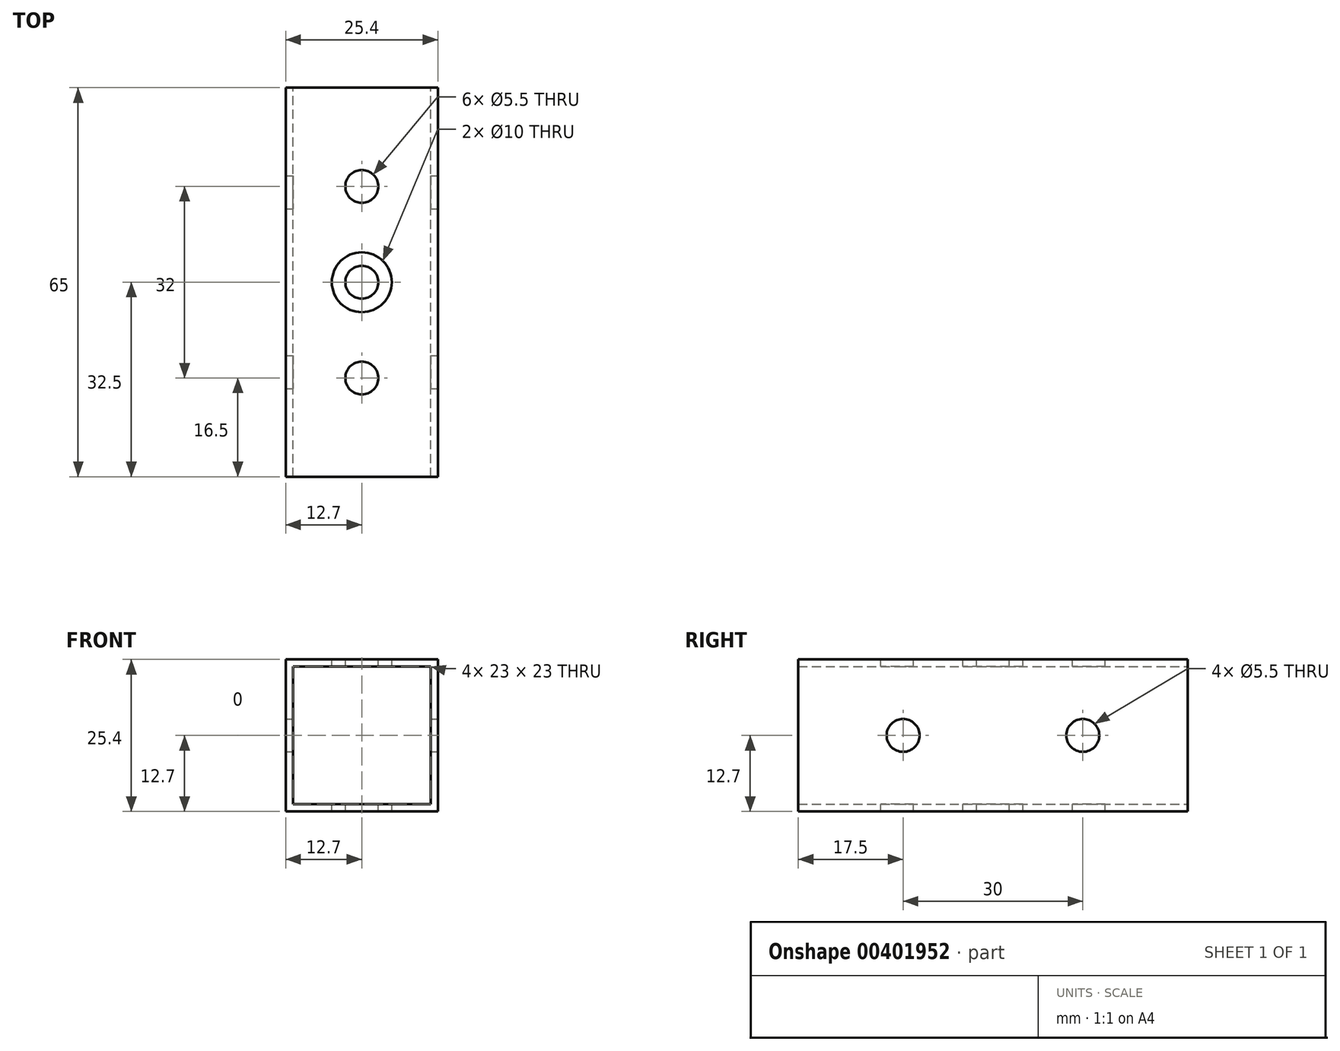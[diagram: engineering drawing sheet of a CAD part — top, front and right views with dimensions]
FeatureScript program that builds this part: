
annotation { "Feature Type Name" : "Feature", "Feature Type Description" : "" }
export const myFeature = defineFeature(function(context is Context, id is Id, definition is map)
    precondition{}
    {
        {
            var Q0;
            Q0=qCreatedBy(makeId("Front.planeOp"),FACE);
            var sketch = newSketch(context, id + "F0", { "sketchPlane" : qUnion([Q0])});
            skLineSegment(sketch, "E0.bottom", {"start": v(-12.7, 12.7) * mm, "end": v(12.7, 12.7) * mm});
            skLineSegment(sketch, "E0.top", {"start": v(-12.7, -12.7) * mm, "end": v(12.7, -12.7) * mm});
            skLineSegment(sketch, "E0.left", {"start": v(-12.7, 12.7) * mm, "end": v(-12.7, -12.7) * mm});
            skLineSegment(sketch, "E0.right", {"start": v(12.7, 12.7) * mm, "end": v(12.7, -12.7) * mm});
            skLineSegment(sketch, "E1", {"start": v(0, 0) * mm, "end": v(0, 12.7) * mm, "construction": true});
            skLineSegment(sketch, "E2", {"start": v(0, 0) * mm, "end": v(-12.7, 0) * mm, "construction": true});
            skLineSegment(sketch, "E3.0", {"start": v(-11.5, -11.5) * mm, "end": v(11.5, -11.5) * mm});
            skLineSegment(sketch, "E3.1", {"start": v(-11.5, 11.5) * mm, "end": v(-11.5, -11.5) * mm});
            skLineSegment(sketch, "E3.2", {"start": v(-11.5, 11.5) * mm, "end": v(11.5, 11.5) * mm});
            skLineSegment(sketch, "E3.3", {"start": v(11.5, 11.5) * mm, "end": v(11.5, -11.5) * mm});
            skSolve(sketch);
        }
        {
            var Q0;
            Q0=qSketchRegion(id+"F0",true);
            var Q1;
            Q1=qConstructionFilter(qBodyType(qCreatedBy(id+"F0",EDGE),BodyType.WIRE),ConstructionObject.NO);
            extrude(context, id + "F1", {"entities" : qUnion([Q0]), "surfaceEntities" : qUnion([Q1]), "endBound" : BoundingType.SYMMETRIC, "depth" : 65 * mm});
        }
        {
            var Q0;
            Q0 = qSketchRegion(id + "F0", true);
            extrude(context, id + "F2", {"entities" : qUnion([Q0]), "endBound" : BoundingType.SYMMETRIC, "depth" : 65 * mm});
        }
        {
            var Q0;
            Q0=makeQuery(id+"F2.opExtrude","SWEPT_FACE",FACE,{"disambiguationData":[OSD([sQuery(id+"F0.wireOp",EDGE,"E0.bottom")])]});
            var sketch = newSketch(context, id + "F3", { "sketchPlane" : qUnion([Q0])});
            skLineSegment(sketch, "E4", {"start": v(0, -32.5) * mm, "end": v(0, -16) * mm});
            skPoint(sketch, "E4.endSnap0", {"position": v(0, -32.5) * mm});
            skLineSegment(sketch, "E5", {"start": v(0, -16) * mm, "end": v(0, 16) * mm});
            skLineSegment(sketch, "E6", {"start": v(0, 16) * mm, "end": v(0, 32.5) * mm});
            skPoint(sketch, "E7", {"position": v(0, 0) * mm});
            skSolve(sketch);
        }
        {
            var Q0;
            Q0=sQuery(id+"F3.wireOp",VERTEX,"E4.end");
            var Q1;
            Q1=sQuery(id+"F3.wireOp",VERTEX,"E6.start");
            var Q2;
            Q2=makeQuery(id+"F2.opExtrude","SWEPT_BODY",BODY,{"disambiguationData":[OSD([sQuery(id+"F0.wireOp",EDGE,"E0.bottom"),sQuery(id+"F0.wireOp",EDGE,"E0.top"),sQuery(id+"F0.wireOp",EDGE,"E0.left"),sQuery(id+"F0.wireOp",EDGE,"E0.right"),sQuery(id+"F0.wireOp",EDGE,"E3.0"),sQuery(id+"F0.wireOp",EDGE,"E3.1"),sQuery(id+"F0.wireOp",EDGE,"E3.2"),sQuery(id+"F0.wireOp",EDGE,"E3.3")])]});
            hole(context, id + "F4", {"style" : HoleStyle.SIMPLE, "endStyle" : HoleEndStyle.THROUGH, "holeDiameter" : 5.5 * mm, "isTappedThrough" : true, "tappedDepth" : 12 * mm, "tapClearance" : 3, "locations" : qUnion([Q0, Q1]), "scope" : qUnion([Q2])});
        }
        {
            var Q0;
            Q0=sQuery(id+"F3.wireOp",VERTEX,"E7");
            var Q1;
            Q1=makeQuery(id+"F2.opExtrude","SWEPT_BODY",BODY,{"disambiguationData":[OSD([sQuery(id+"F0.wireOp",EDGE,"E0.bottom"),sQuery(id+"F0.wireOp",EDGE,"E0.top"),sQuery(id+"F0.wireOp",EDGE,"E0.left"),sQuery(id+"F0.wireOp",EDGE,"E0.right"),sQuery(id+"F0.wireOp",EDGE,"E3.0"),sQuery(id+"F0.wireOp",EDGE,"E3.1"),sQuery(id+"F0.wireOp",EDGE,"E3.2"),sQuery(id+"F0.wireOp",EDGE,"E3.3")])]});
            hole(context, id + "F5", {"style" : HoleStyle.SIMPLE, "endStyle" : HoleEndStyle.THROUGH, "holeDiameter" : 10 * mm, "isTappedThrough" : true, "tappedDepth" : 12 * mm, "tapClearance" : 3, "locations" : qUnion([Q0]), "scope" : qUnion([Q1])});
        }
        {
            var Q0;
            Q0 = qSketchRegion(id + "F0", true);
            extrude(context, id + "F6", {"entities" : qUnion([Q0]), "endBound" : BoundingType.SYMMETRIC, "depth" : 65 * mm});
        }
        {
            var Q0;
            Q0=makeQuery(id+"F6.opExtrude","SWEPT_FACE",FACE,{"disambiguationData":[OSD([sQuery(id+"F0.wireOp",EDGE,"E0.right")])]});
            var sketch = newSketch(context, id + "F7", { "sketchPlane" : qUnion([Q0])});
            skLineSegment(sketch, "E8", {"start": v(-15, 0) * mm, "end": v(0, 0) * mm});
            skLineSegment(sketch, "E9", {"start": v(0, 0) * mm, "end": v(15, 0) * mm});
            skSolve(sketch);
        }
        {
            var Q0;
            Q0=sQuery(id+"F7.wireOp",VERTEX,"E8.start");
            var Q1;
            Q1=sQuery(id+"F7.wireOp",VERTEX,"E9.end");
            var Q2;
            Q2=makeQuery(id+"F6.opExtrude","SWEPT_BODY",BODY,{"disambiguationData":[OSD([sQuery(id+"F0.wireOp",EDGE,"E0.bottom"),sQuery(id+"F0.wireOp",EDGE,"E0.top"),sQuery(id+"F0.wireOp",EDGE,"E0.left"),sQuery(id+"F0.wireOp",EDGE,"E0.right"),sQuery(id+"F0.wireOp",EDGE,"E3.0"),sQuery(id+"F0.wireOp",EDGE,"E3.1"),sQuery(id+"F0.wireOp",EDGE,"E3.2"),sQuery(id+"F0.wireOp",EDGE,"E3.3")])]});
            hole(context, id + "F8", {"style" : HoleStyle.SIMPLE, "endStyle" : HoleEndStyle.THROUGH, "holeDiameter" : 5.5 * mm, "isTappedThrough" : true, "tappedDepth" : 12 * mm, "tapClearance" : 3, "locations" : qUnion([Q0, Q1]), "scope" : qUnion([Q2])});
        }
        {
            var Q0;
            Q0 = qSketchRegion(id + "F0", true);
            extrude(context, id + "F9", {"entities" : qUnion([Q0]), "endBound" : BoundingType.SYMMETRIC, "depth" : 65 * mm});
        }
        {
            var Q0;
            Q0=makeQuery(id+"F9.opExtrude","SWEPT_FACE",FACE,{"disambiguationData":[OSD([sQuery(id+"F0.wireOp",EDGE,"E0.bottom")])]});
            var sketch = newSketch(context, id + "F10", { "sketchPlane" : qUnion([Q0])});
            skLineSegment(sketch, "E10", {"start": v(0, -32.5) * mm, "end": v(0, 32.5) * mm, "construction": true});
            skPoint(sketch, "E11", {"position": v(0, 0) * mm});
            skSolve(sketch);
        }
        {
            var Q0;
            Q0=sQuery(id+"F10.wireOp",VERTEX,"E11");
            var Q1;
            Q1=makeQuery(id+"F9.opExtrude","SWEPT_BODY",BODY,{"disambiguationData":[OSD([sQuery(id+"F0.wireOp",EDGE,"E0.bottom"),sQuery(id+"F0.wireOp",EDGE,"E0.top"),sQuery(id+"F0.wireOp",EDGE,"E0.left"),sQuery(id+"F0.wireOp",EDGE,"E0.right"),sQuery(id+"F0.wireOp",EDGE,"E3.0"),sQuery(id+"F0.wireOp",EDGE,"E3.1"),sQuery(id+"F0.wireOp",EDGE,"E3.2"),sQuery(id+"F0.wireOp",EDGE,"E3.3")])]});
            hole(context, id + "F11", {"style" : HoleStyle.SIMPLE, "endStyle" : HoleEndStyle.THROUGH, "holeDiameter" : 5.5 * mm, "isTappedThrough" : true, "tappedDepth" : 12 * mm, "tapClearance" : 3, "locations" : qUnion([Q0]), "scope" : qUnion([Q1])});
        }
    });
